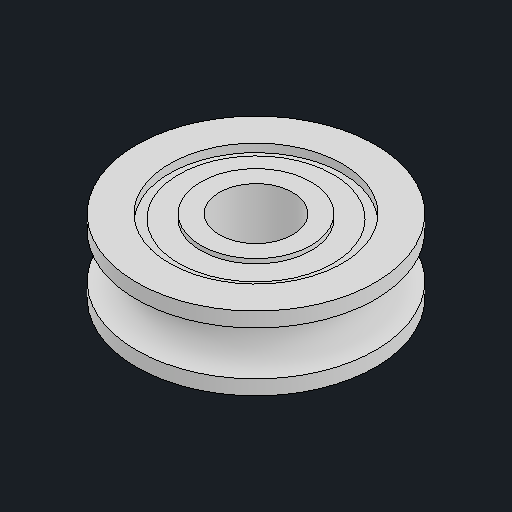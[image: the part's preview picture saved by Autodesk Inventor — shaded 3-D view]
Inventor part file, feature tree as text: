
AUTODESK INVENTOR PART (.ipt)
format: ipt  version: 2024.2 (Build 282272000, 272)  size: 139,264 bytes
history: native  units: mm
features: other x1, mirror x1
ambient origin geometry x8: Origin, YZ Plane, XZ Plane, XY Plane, X Axis, Y Axis, Z Axis, Center Point
bodies: Body1 (feature_tree)
feature tree (2):
  other  "솔리드1"
  mirror  "Mirror1"
